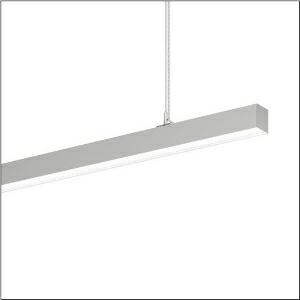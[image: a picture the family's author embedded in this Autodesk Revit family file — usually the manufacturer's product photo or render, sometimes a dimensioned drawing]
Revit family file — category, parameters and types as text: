
# Revit family: silica_r__21_51mx30tbt5s_71cb
name_source: partatom
category: Lighting Fixtures
units: mm (PartAtom-declared; Revit-internal decimal feet)

## family parameters
Cut with Voids When Loaded = No
Host = Face
Light Source = No
Part Type = Normal
Room Calculation Point = No
Round Connector Dimension = Use Diameter
Shared = No

## types (1)
- --- (1 x LED, 5150 lm, 42.2 W, 6500K)
    Apparent Load = 42 VA
    CIE Flux Codes = 47 79 96 58 100
    Color Rendering = 80
    Color Temperature = 6500K
    Default Elevation = 1800 mm
    Description = Silica® 21, office luminaire, primary optical cover: cover, of PMMA, opal, light emission: direct/indirect distribution, primary light characteristic: symmetric, installation type: suspended mounting, LED, rated luminous flux: 5.150lm, luminous efficacy: 116lm/W, light colour: 8tw, colour temperature: 2700..6500K, control gear: DALI DT8, with terminal, 3+2-pole, max. 2.5mm², mains connection: 220..240V, AC, 50/60Hz, rated input power: 44.3W, luminaire housing, of aluminium, metallic grey (RAL 9006), length: 1.504mm, width: 53mm, height: 53mm, protection rating (complete): IP20, insulation class (complete): insulation class I (protective earthing), certification: CE, permissible operating ambient temperature: 0..+35°C, standard: EN 50419, packaging unit: 1 piece
    Height = 53 mm
    Lamp = 1 x LED
    Lamp Light Flux = 5150 lm
    Lamp Power = 42.2 W
    Lamp count = 1
    Length = 1504 mm
    Luminous efficacy = 122 lm/W
    Manufacturer = Siteco
    ModVariant = No
    Model = 51MX30TBT5S
    Mounting Place = Ceiling
    Mounting Type = Pendant
    Number of Poles = 1
    OnlyDefault = Yes
    Power Factor = 1
    Product Name = Silica® 21
    Product group = office luminaire | ceiling pendant
    ProductGroupID = 904
    Protection Class = Protection class I
    Protection Degree = IP 20
    RLX_Detail_Level = 1
    RLX_Emergency_Light_Flux = 0 lm
    RLX_Emergency_Type = 0
    RLX_Emergency_Type_DB = No
    RlxData = <blob elided: 20173 chars, md5=e89eae93>
    Socket = socket
    Standby Power = 0 W
    System Light Flux = 5150 lm
    System Power = 42 W
    Type Comments = individual setting
    Type Image = l_1335864.jpg
    URL = http://relux.com
    VarID = @adj_139614
    Voltage = 0 V
    Weight = 0.00 kg
    Width = 53 mm

## geometry (parser evidence)
native form markers: Blend x4, Sweep x13
no freeform markers — native parametric forms only
